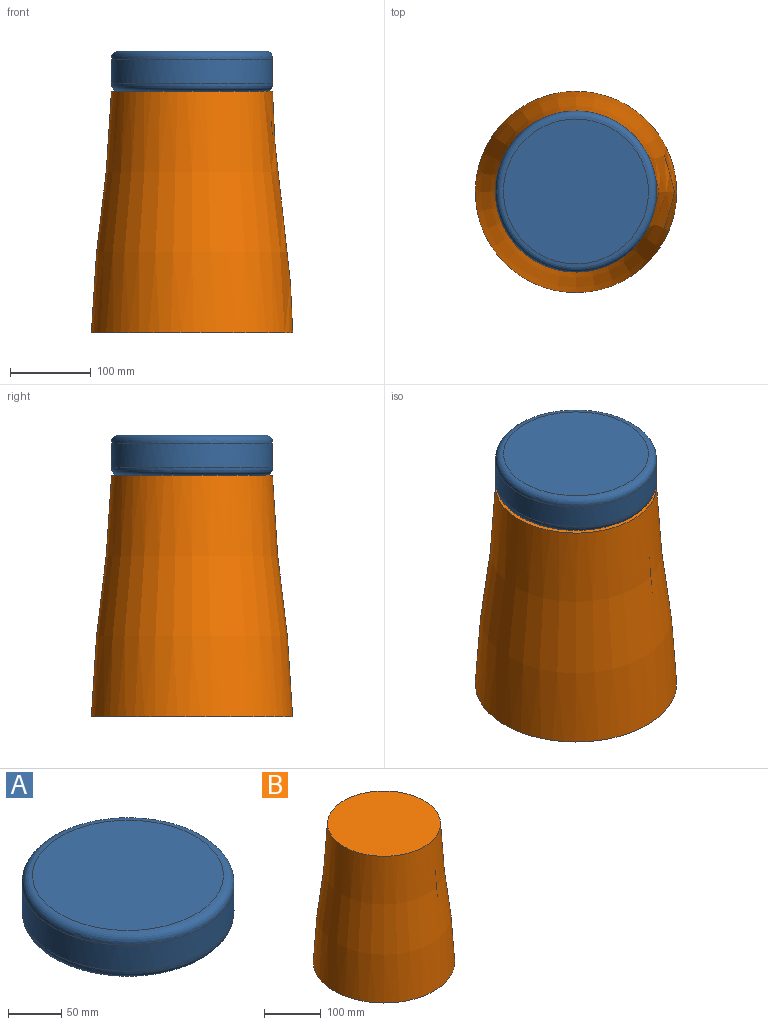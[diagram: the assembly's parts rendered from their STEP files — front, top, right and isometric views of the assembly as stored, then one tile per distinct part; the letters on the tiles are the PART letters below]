
ASSEMBLY  parts=2 mates=1
PART A: 5 faces, bbox 201.3x201.3x50 mm
  f0: cylinder r=100mm len=200mm, axis (0,0,-1), area 18849.6mm2, adj f3,f4
  f1: plane 180.01x180.01mm, normal (0,0,1), area 25444.9mm2, adj f3
  f2: plane 180.01x180.01mm, normal (0,0,-1), area 25444.9mm2, adj f4
  f3: bspline ~201.29x201.29mm, area 9870.1mm2, adj f0,f1
  f4: bspline ~201.29x201.29mm, area 9870.1mm2, adj f0,f2
PART B: 5 faces, bbox 1682.7x1375x1300.6 mm
  f0: plane 200.01x200.01mm, normal (0,0,1), area 31413.5mm2, adj f1
  f1: bspline ~300x250mm, area 212938.1mm2, adj f0,f2
  f2: plane 1250.63x1250.63mm, normal (0,0,-1), area 1960mm2, adj f1,f4
  f3: plane 996.17x996.15mm, normal (0,0,-1), area 29855.7mm2, adj f4
  f4: offset ~686.82x372.32mm, area 337700.6mm2, adj f2,f3
PLACE A t=(-56.36,29.3,243.67)mm
PLACE B t=(-56.36,29.3,-56.33)mm
MATE parallel A.f0 <-> B.f0  axis (0,0,-1) through (-56.36,29.3,243.67)mm
